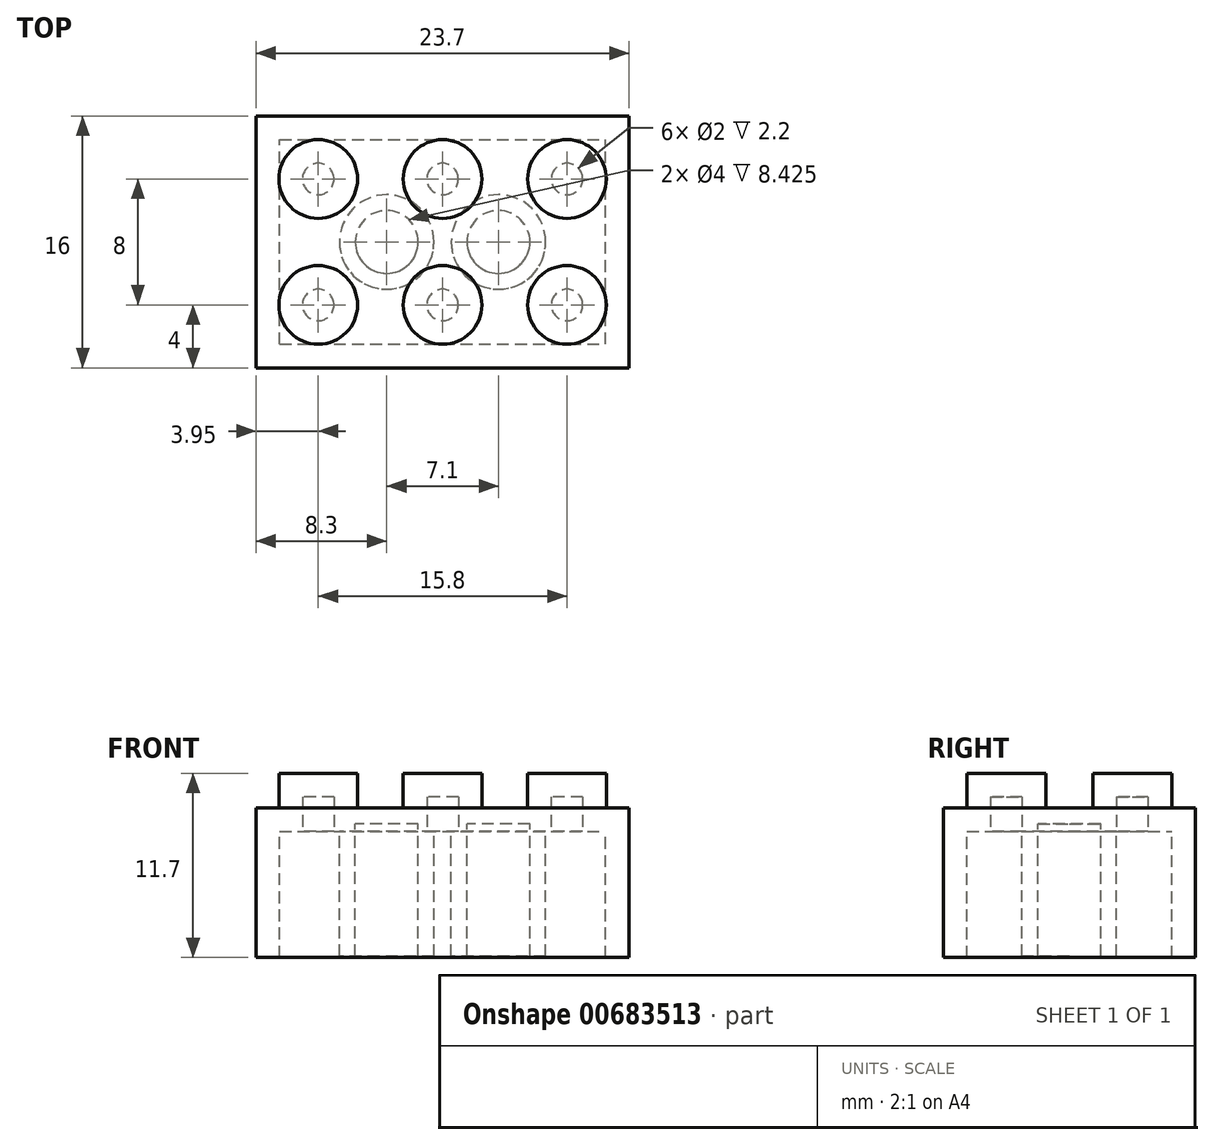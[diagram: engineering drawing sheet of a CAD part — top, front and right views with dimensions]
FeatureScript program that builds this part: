
annotation { "Feature Type Name" : "Feature", "Feature Type Description" : "" }
export const myFeature = defineFeature(function(context is Context, id is Id, definition is map)
    precondition{}
    {
        {
            var Q0;
            Q0=qCreatedBy(makeId("Top.planeOp"),FACE);
            var sketch = newSketch(context, id + "F0", { "sketchPlane" : qUnion([Q0])});
            skLineSegment(sketch, "E0.bottom", {"start": v(0, 0) * mm, "end": v(23.7, 0) * mm});
            skLineSegment(sketch, "E0.top", {"start": v(0, 8) * mm, "end": v(23.7, 8) * mm});
            skLineSegment(sketch, "E0.left", {"start": v(0, 0) * mm, "end": v(0, 8) * mm});
            skLineSegment(sketch, "E0.right", {"start": v(23.7, 0) * mm, "end": v(23.7, 8) * mm});
            skPoint(sketch, "E1", {"position": v(0, 4) * mm});
            skLineSegment(sketch, "E2", {"start": v(0, 4) * mm, "end": v(23.7, 4) * mm, "construction": true});
            skPoint(sketch, "E3", {"position": v(11.85, 8) * mm});
            skLineSegment(sketch, "E4", {"start": v(11.85, 8) * mm, "end": v(11.85, 0) * mm, "construction": true});
            skCircle(sketch, "E5", {"center": v(11.85, 4) * mm, "radius": 2.5 * mm});
            skCircle(sketch, "E6", {"center": v(19.75, 4) * mm, "radius": 2.5 * mm});
            skCircle(sketch, "E7", {"center": v(3.95, 4) * mm, "radius": 2.5 * mm});
            skSolve(sketch);
        }
        {
            var Q0;
            Q0=makeQuery(id+"F0.imprint","IMPRINT",FACE,{"disambiguationData":[TD([[makeQuery(id+"F0.imprint","IMPRINT",EDGE,{"derivedFrom":sQuery(id+"F0.wireOp",EDGE,"E6")}),1.0]])]});
            var Q1;
            Q1=makeQuery(id+"F0.imprint","IMPRINT",FACE,{"disambiguationData":[TD([[makeQuery(id+"F0.imprint","IMPRINT",EDGE,{"derivedFrom":sQuery(id+"F0.wireOp",EDGE,"E5")}),1.0]])]});
            var Q2;
            Q2=makeQuery(id+"F0.imprint","IMPRINT",FACE,{"disambiguationData":[TD([[makeQuery(id+"F0.imprint","IMPRINT",EDGE,{"derivedFrom":sQuery(id+"F0.wireOp",EDGE,"E7")}),1.0]])]});
            var Q3;
            Q3=makeQuery(id+"F0.imprint","IMPRINT",FACE,{"disambiguationData":[TD([[makeQuery(id+"F0.imprint","IMPRINT",EDGE,{"derivedFrom":sQuery(id+"F0.wireOp",EDGE,"E0.bottom")}),1.0]])]});
            extrude(context, id + "F1", {"entities" : qUnion([Q0, Q1, Q2, Q3]), "oppositeDirection" : true, "depth" : 9.5 * mm, "offsetDistance" : 25.4 * mm});
        }
        {
            var Q0;
            Q0=makeQuery(id+"F0.imprint","IMPRINT",FACE,{"disambiguationData":[TD([[makeQuery(id+"F0.imprint","IMPRINT",EDGE,{"derivedFrom":sQuery(id+"F0.wireOp",EDGE,"E7")}),1.0]])]});
            var Q1;
            Q1=makeQuery(id+"F0.imprint","IMPRINT",FACE,{"disambiguationData":[TD([[makeQuery(id+"F0.imprint","IMPRINT",EDGE,{"derivedFrom":sQuery(id+"F0.wireOp",EDGE,"E5")}),1.0]])]});
            var Q2;
            Q2=makeQuery(id+"F0.imprint","IMPRINT",FACE,{"disambiguationData":[TD([[makeQuery(id+"F0.imprint","IMPRINT",EDGE,{"derivedFrom":sQuery(id+"F0.wireOp",EDGE,"E6")}),1.0]])]});
            extrude(context, id + "F2", {"entities" : qUnion([Q0, Q1, Q2]), "operationType" : NewBodyOperationType.ADD, "depth" : 2.2 * mm, "offsetDistance" : 25.4 * mm});
        }
        {
            var Q0;
            Q0=makeQuery(id+"F1.opExtrude","SWEPT_BODY",BODY,{"disambiguationData":[OSD([sQuery(id+"F0.wireOp",EDGE,"E0.bottom"),sQuery(id+"F0.wireOp",EDGE,"E0.top"),sQuery(id+"F0.wireOp",EDGE,"E0.left"),sQuery(id+"F0.wireOp",EDGE,"E0.right")])]});
            var Q1;
            Q1=makeQuery(id+"F1.opExtrude","SWEPT_FACE",FACE,{"disambiguationData":[OSD([sQuery(id+"F0.wireOp",EDGE,"E0.bottom")])]});
            mirror(context, id + "F3", {"operationType" : NewBodyOperationType.ADD, "entities" : qUnion([Q0]), "mirrorPlane" : qUnion([Q1])});
        }
        {
            var Q0;
            {var subQ0=makeQuery(id+"F1.opExtrude","CAP_FACE",FACE,{"disambiguationData":[OSD([sQuery(id+"F0.wireOp",EDGE,"E0.bottom"),sQuery(id+"F0.wireOp",EDGE,"E0.top"),sQuery(id+"F0.wireOp",EDGE,"E0.left"),sQuery(id+"F0.wireOp",EDGE,"E0.right")])],"isStart":false});Q0=makeQuery(id+"F3.boolean.opBoolean","MERGE",FACE,{"derivedFrom":[subQ0,makeQuery(id+"F3.opPattern","COPY",FACE,{"derivedFrom":subQ0,"instanceName":"1"})]});}
            shell(context, id + "F4", {"entities" : qUnion([Q0]), "thickness" : 1.5 * mm});
        }
        {
            var Q0;
            Q0=makeQuery(id+"F4.opShell","OFFSET_FACE",FACE,{"disambiguationData":[OSD([sQuery(id+"F0.wireOp",EDGE,"E0.bottom"),sQuery(id+"F0.wireOp",EDGE,"E0.top"),sQuery(id+"F0.wireOp",EDGE,"E0.left"),sQuery(id+"F0.wireOp",EDGE,"E0.right")])]});
            var sketch = newSketch(context, id + "F5", { "sketchPlane" : qUnion([Q0])});
            skLineSegment(sketch, "E8", {"start": v(22.2, 0) * mm, "end": v(1.5, 0) * mm, "construction": true});
            skCircle(sketch, "E9", {"center": v(8.3, 0) * mm, "radius": 3 * mm});
            skCircle(sketch, "E10", {"center": v(15.4, 0) * mm, "radius": 3 * mm});
            skSolve(sketch);
        }
        {
            var Q0;
            Q0=qSketchRegion(id+"F5",true);
            extrude(context, id + "F6", {"entities" : qUnion([Q0]), "operationType" : NewBodyOperationType.ADD, "depth" : 7.92 * mm, "offsetDistance" : 25.4 * mm});
        }
        {
            var Q0;
            Q0=makeQuery(id+"F6.opExtrude","CAP_FACE",FACE,{"disambiguationData":[OSD([sQuery(id+"F5.wireOp",EDGE,"E10")])],"isStart":false});
            var Q1;
            Q1=makeQuery(id+"F6.opExtrude","CAP_FACE",FACE,{"disambiguationData":[OSD([sQuery(id+"F5.wireOp",EDGE,"E9")])],"isStart":false});
            shell(context, id + "F7", {"entities" : qUnion([Q0, Q1]), "thickness" : 1 * mm});
        }
    });
